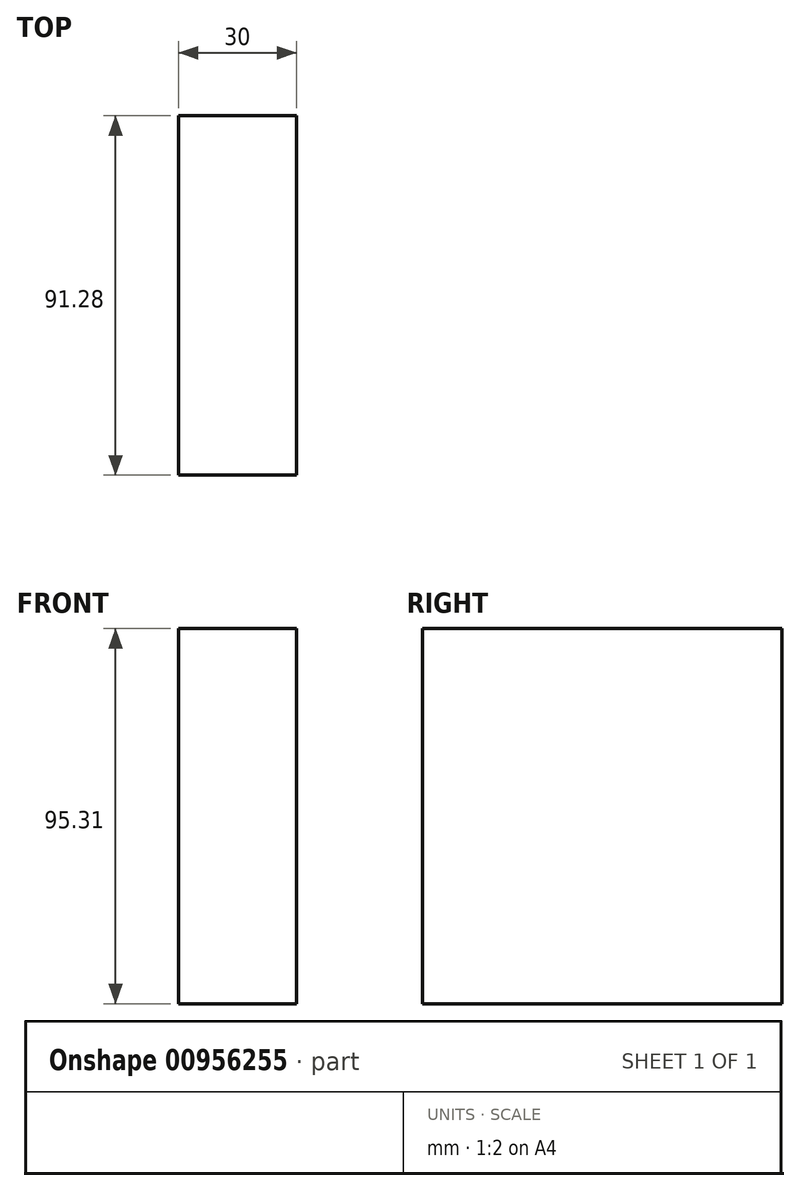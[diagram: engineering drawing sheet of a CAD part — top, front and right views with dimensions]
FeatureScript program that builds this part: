
annotation { "Feature Type Name" : "Feature", "Feature Type Description" : "" }
export const myFeature = defineFeature(function(context is Context, id is Id, definition is map)
    precondition{}
    {
        {
            var Q0;
            Q0=qCreatedBy(makeId("Right.planeOp"),FACE);
            var sketch = newSketch(context, id + "F0", { "sketchPlane" : qUnion([Q0])});
            skLineSegment(sketch, "E0.bottom", {"start": v(-43.02, 40.6) * mm, "end": v(48.26, 40.6) * mm});
            skLineSegment(sketch, "E0.top", {"start": v(-43.02, -54.72) * mm, "end": v(48.26, -54.72) * mm});
            skLineSegment(sketch, "E0.left", {"start": v(-43.02, 40.6) * mm, "end": v(-43.02, -54.72) * mm});
            skLineSegment(sketch, "E0.right", {"start": v(48.26, 40.6) * mm, "end": v(48.26, -54.72) * mm});
            skSolve(sketch);
        }
        {
            var Q0;
            Q0=makeQuery(id+"F0.imprint","IMPRINT",FACE,{"disambiguationData":[TD([[makeQuery(id+"F0.imprint","IMPRINT",EDGE,{"derivedFrom":sQuery(id+"F0.wireOp",EDGE,"E0.bottom")}),-1.0]])]});
            extrude(context, id + "F1", {"entities" : qUnion([Q0]), "depth" : 30 * mm, "offsetDistance" : 25.4 * mm});
        }
    });
